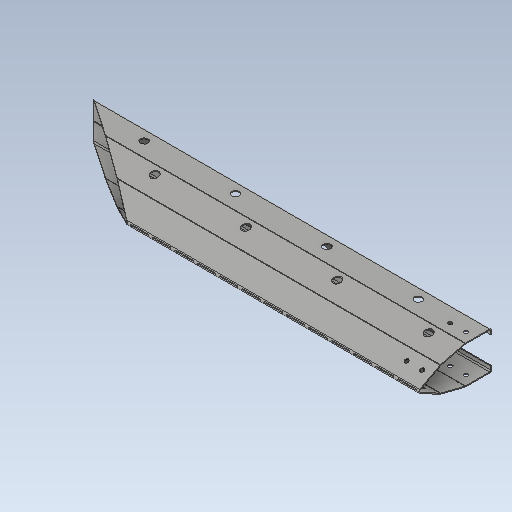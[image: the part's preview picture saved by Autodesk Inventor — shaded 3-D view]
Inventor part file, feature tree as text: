
AUTODESK INVENTOR PART (.ipt)
format: ipt  version: 2020.1 (Build 241239000, 239)  size: 871,936 bytes
history: native  units: mm
features: reference x24, sketch x22, other x20, hole x16, sheet_metal_op x13, plane x9, projected_geometry x7, extrude x4
ambient origin geometry x8: Origin, YZ Plane, XZ Plane, XY Plane, X Axis, Y Axis, Z Axis, Center Point
bodies: Solid1 (feature_tree)
feature tree (115):
  plane  "Work Plane1"
  sheet_metal_op  "Face1"
  plane  "Work Plane2"
  sheet_metal_op  "Face2"
  plane  "Work Plane3"
  sheet_metal_op  "Face3"
  plane  "Work Plane4"
  sheet_metal_op  "Face4"
  plane  "Work Plane5"
  sheet_metal_op  "Face5"
  plane  "Work Plane6"
  sheet_metal_op  "Face6"
  plane  "Work Plane7"
  sheet_metal_op  "Face7"
  other  "midtplan"
  extrude  "Extrusion3"  Depth=3.75mm
  extrude  "hulsæt til stifter"  Depth=3.0mm
  plane  "Work Plane11"
  sketch  "Sketch13"  dims[d18=1.5mm d19=6.0mm]
  plane  "Work Plane12"
  extrude  "balusterhul"  Depth=3.75mm
  extrude  "balusterhul skråkompensering"  Depth=3.0mm
  hole  "Hole2"  [1 undecoded]
  hole  "Hole4"  [1 undecoded]
  hole  "Hole6"  [1 undecoded]
  hole  "Hole8"  [1 undecoded]
  hole  "Hole10"  [1 undecoded]
  hole  "Hole12"  [1 undecoded]
  hole  "Hole14"  [1 undecoded]
  hole  "Hole16"  [1 undecoded]
  sketch  "Sketch1"  dims[d0=3.0mm d1=3.75mm]
  reference  "Reference1"
  reference  "Reference2"
  reference  "Reference3"
  reference  "Reference4"
  other  "Plate1"
  sketch  "Sketch2"  dims[d2=3.0mm d3=1.5mm]
  reference  "Reference5"
  reference  "Reference6"
  reference  "Reference7"
  reference  "Reference8"
  other  "Plate2"
  sheet_metal_op  "Bend1"
  sketch  "Sketch3"  dims[d4=6.0mm d5=3.75mm]
  reference  "Reference9"
  reference  "Reference10"
  reference  "Reference11"
  other  "Plate3"
  sheet_metal_op  "Bend2"
  sketch  "Sketch4"  dims[d6=3.75mm d7=3.0mm]
  reference  "Reference12"
  reference  "Reference13"
  reference  "Reference14"
  reference  "Reference15"
  other  "Plate4"
  sheet_metal_op  "Bend3"
  sketch  "Sketch5"  dims[d8=1.5mm d9=6.0mm]
  reference  "Reference16"
  reference  "Reference17"
  reference  "Reference18"
  other  "Plate5"
  sheet_metal_op  "Bend4"
  sketch  "Sketch6"  dims[d10=3.75mm d11=3.75mm]
  reference  "Reference19"
  reference  "Reference20"
  reference  "Reference21"
  other  "Plate6"
  sheet_metal_op  "Bend5"
  sketch  "Sketch7"  dims[d12=3.0mm d13=1.5mm]
  reference  "Reference22"
  reference  "Reference23"
  other  "Plate7"
  sheet_metal_op  "Bend6"
  sketch  "Sketch8"  dims[d14=6.0mm d15=3.75mm]
  reference  "Reference24"
  projected_geometry  "Projected Loop1"
  other  "huller til stifter"
  projected_geometry  "Projected Loop3"
  sketch  "Sketch12"  dims[d16=3.75mm d17=3.0mm]
  projected_geometry  "Projected Loop4"
  sketch  "Sketch14"  dims[d20=3.75mm d21=3.75mm]
  sketch  "Sketch15"  dims[d22=3.0mm d23=1.5mm]
  projected_geometry  "Projected Loop5"
  projected_geometry  "Projected Loop6"
  sketch  "Sketch16"  dims[d24=6.0mm d25=3.75mm]
  projected_geometry  "Projected Loop7"
  projected_geometry  "Projected Loop8"
  sketch  "Sketch17"  dims[d26=3.75mm d27=3.0mm]
  sketch  "Sketch18"  dims[d28=1.5mm d29=6.0mm]
  hole  "Hole1"  [1 undecoded]
  sketch  "Sketch19"  dims[d30=3.75mm d31=3.0mm]
  hole  "Hole3"  [1 undecoded]
  sketch  "Sketch20"  dims[d32=0.0mm d33=3.0mm]
  hole  "Hole5"  [1 undecoded]
  sketch  "Sketch21"  dims[d39=250.0mm d41=33.7mm]
  hole  "Hole7"  [1 undecoded]
  sketch  "Sketch22"  dims[d42=33.7mm d43=60.0mm d44=60.0mm]
  hole  "Hole9"  [1 undecoded]
  sketch  "Sketch23"  dims[d45=16.85mm d46=65.0mm]
  hole  "Hole11"  [1 undecoded]
  sketch  "Sketch24"  dims[d47=60.0mm]
  hole  "Hole13"  [1 undecoded]
  sketch  "Sketch25"  dims[d48=10.0mm d49=0.0mm d69=10.0mm d70=0.0mm d73=96.672mm d75=5.986479mm d76=180.0mm d77=26.6mm d78=25.8mm d79=40.0mm d81=302.737mm d82=10.0mm d84=10.0mm d86=90.0deg d87=113.655385mm d88=56.827692mm d89=90.0deg d90=49.0mm d91=100.0mm d92=0.0mm d95=100.0mm d96=0.0mm d97=2.046461mm d99=1.023231mm d100=90.0mm d101=30.0mm d102=30.0mm d103=342.765mm d104=342.765mm d105=30.0mm d106=342.765mm d107=10.0mm d108=3.0mm d109=0.0mm d110=8.0mm d111=6.0mm d112=61.6mm d113=140.0mm d115=73.92mm d116=10.0mm d118=10.0mm d120=3.0mm d121=0.0mm d122=13.5mm d123=6.0mm d124=4.0mm d125=2.0mm d126=90.0deg d127=8.0mm d128=0.0mm d129=13.5mm d130=6.0mm d131=4.0mm d132=2.0mm d133=90.0deg d134=8.0mm d135=0.0mm d136=13.5mm d137=6.0mm d138=4.0mm d139=2.0mm d140=90.0deg d141=8.0mm d142=0.0mm d143=13.5mm d144=6.0mm d145=4.0mm d146=2.0mm d147=90.0deg d148=8.0mm d149=0.0mm d150=13.5mm d151=6.0mm d152=4.0mm d153=2.0mm d154=90.0deg d155=8.0mm d156=0.0mm d157=13.5mm d158=6.0mm d159=4.0mm d160=2.0mm d161=90.0deg d162=8.0mm d163=0.0mm d164=13.5mm d165=6.0mm d166=4.0mm d167=2.0mm d168=90.0deg d169=8.0mm d170=0.0mm d171=13.5mm d172=6.0mm d173=4.0mm d174=2.0mm d175=90.0deg d176=8.0mm d177=0.0mm d178=1.0mm d179=1.0mm]
  hole  "Hole15"  [1 undecoded]
  other  "Cut1"
  other  "plantehuller"
  other  "bukkeperforering"
  parser-record x3  (decoder bookkeeping rows leaked as tree rows — omitted from the tree; the rows remain in map.json)
  other  "modul bund.iam"
  other  "model:1"
  other  "Definition1"
  other  "modul.iam"
  other  "modul top.iam"
note: 16 required parameter values undecoded (feature->parameter linkage not recoverable at this tier; creation-order binding heuristic only, values carry confidence <= 0.55)
note: 3 file-system paths scrubbed to <path> (originals preserved in map.json)
